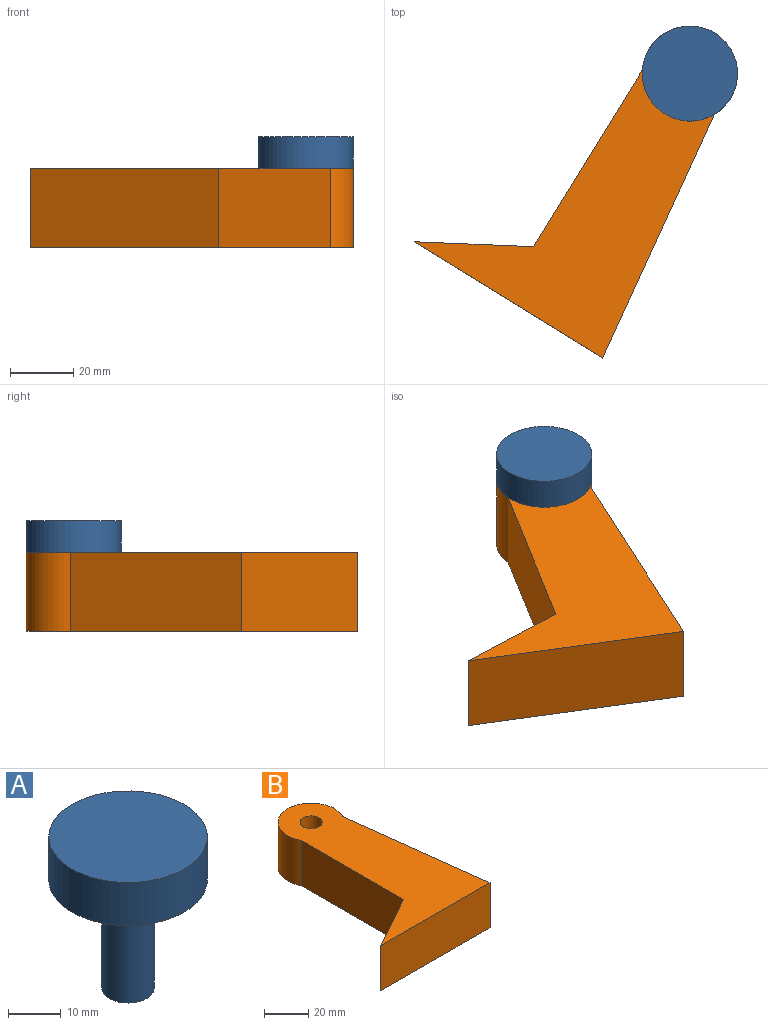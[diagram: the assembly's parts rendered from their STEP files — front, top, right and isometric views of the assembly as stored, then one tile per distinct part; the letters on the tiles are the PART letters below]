
ASSEMBLY  parts=2 mates=1
PART A: 5 faces, bbox 30x30x35 mm
  f0: cylinder r=5mm len=25mm, axis (0,0,-1), area 785.4mm2, adj f1,f4
  f1: plane 10x10mm, normal (0,0,-1), area 78.5mm2, adj f0
  f2: cylinder r=15mm len=30mm, axis (0,0,-1), area 942.5mm2, adj f3,f4
  f3: plane 30x30mm, normal (0,0,1), area 706.9mm2, adj f2
  f4: plane 30x30mm, normal (0,0,-1), area 628.3mm2, adj f0,f2
PART B: 8 faces, bbox 69.7x105.7x25 mm
  f0: cylinder r=15mm len=30mm, axis (0,0,-1), area 1535.5mm2, adj f1,f4,f5,f6
  f1: plane 65.46x25mm, normal (-1,0,0), area 1636.6mm2, adj f0,f2,f5,f6
  f2: plane 32.73x25mm, normal (-0.49,0.87,0), area 938.5mm2, adj f1,f3,f5,f6
  f3: plane 69.73x25mm, normal (0,-1,0), area 1743.3mm2, adj f2,f4,f5,f6
  f4: plane 83.84x25mm, normal (0.99,0.12,0), area 2111.9mm2, adj f0,f3,f5,f6
  f5: plane 105.72x69.73mm, normal (0,0,1), area 3443.1mm2, adj f0,f1,f2,f3,f4,f7
  f6: plane 105.72x69.73mm, normal (0,0,-1), area 3443.1mm2, adj f0,f1,f2,f3,f4,f7
  f7: cylinder r=5mm len=25mm, axis (0,0,1), area 785.4mm2, adj f5,f6
PLACE A t=(44.07,-46.84,77.54)mm fixed
PLACE B rot(axis=(0,0,-1),31.7deg) t=(44.07,-46.84,77.54)mm
MATE revolute B.f0 <-> A.f0  axis (0,0,-1) through (44.07,-46.84,77.54)mm
